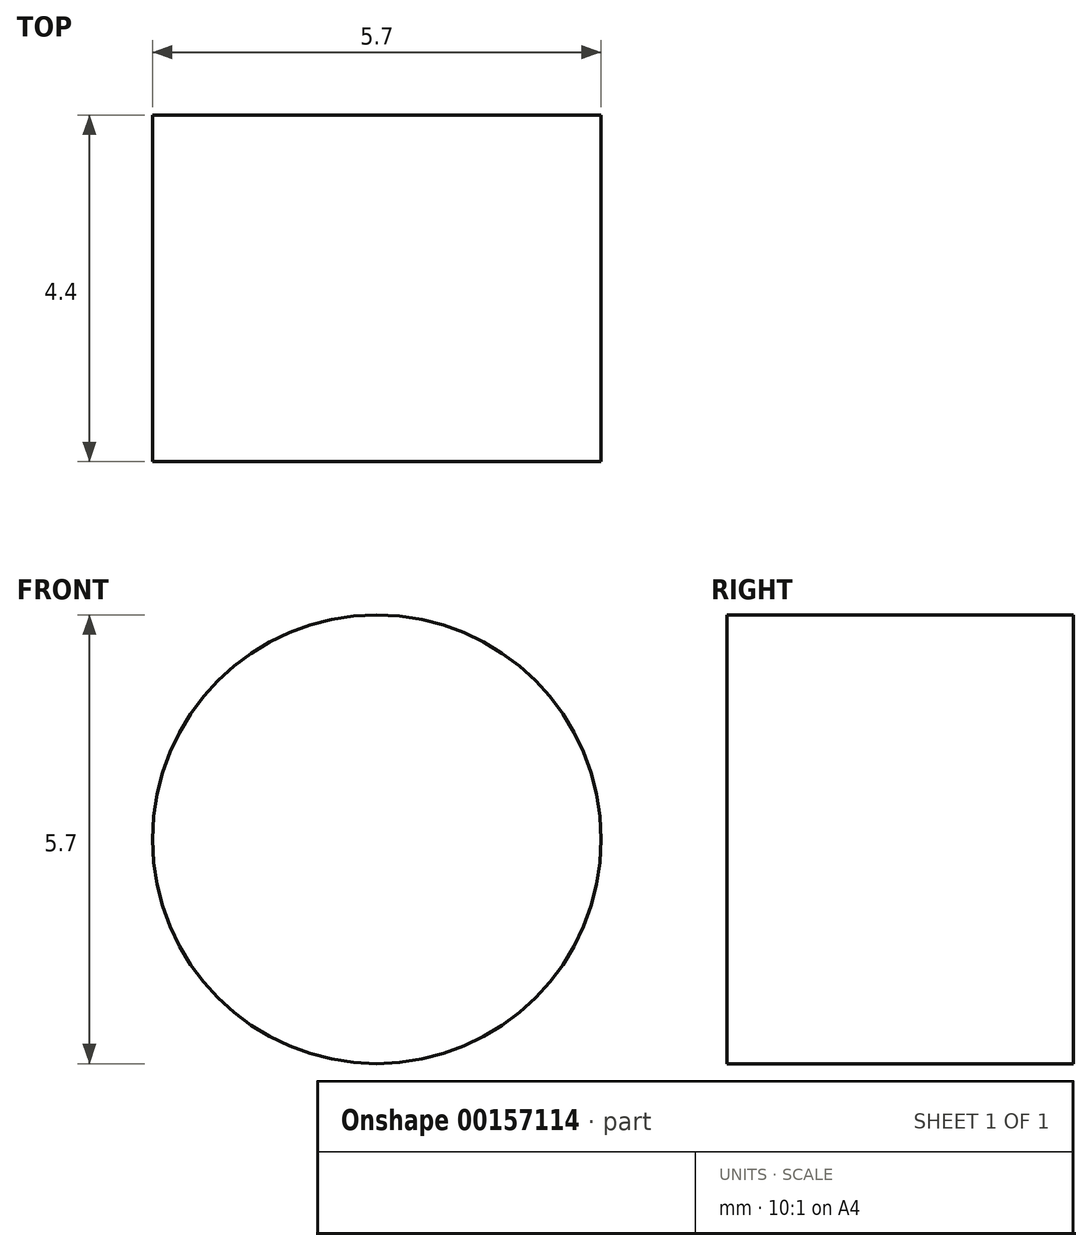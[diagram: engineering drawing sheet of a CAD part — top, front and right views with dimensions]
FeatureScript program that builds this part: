
annotation { "Feature Type Name" : "Feature", "Feature Type Description" : "" }
export const myFeature = defineFeature(function(context is Context, id is Id, definition is map)
    precondition{}
    {
        {
            var Q0;
            Q0=qCreatedBy(makeId("Front.planeOp"),FACE);
            var sketch = newSketch(context, id + "F0", { "sketchPlane" : qUnion([Q0])});
            skCircle(sketch, "E0", {"center": v(0, 0) * mm, "radius": 2.85 * mm});
            skSolve(sketch);
        }
        {
            var Q0;
            Q0=makeQuery(id+"F0.imprint","IMPRINT",FACE,{"disambiguationData":[TD([[makeQuery(id+"F0.imprint","IMPRINT",EDGE,{"derivedFrom":sQuery(id+"F0.wireOp",EDGE,"E0")}),1.0]])]});
            extrude(context, id + "F1", {"entities" : qUnion([Q0]), "depth" : 4.4 * mm});
        }
    });
